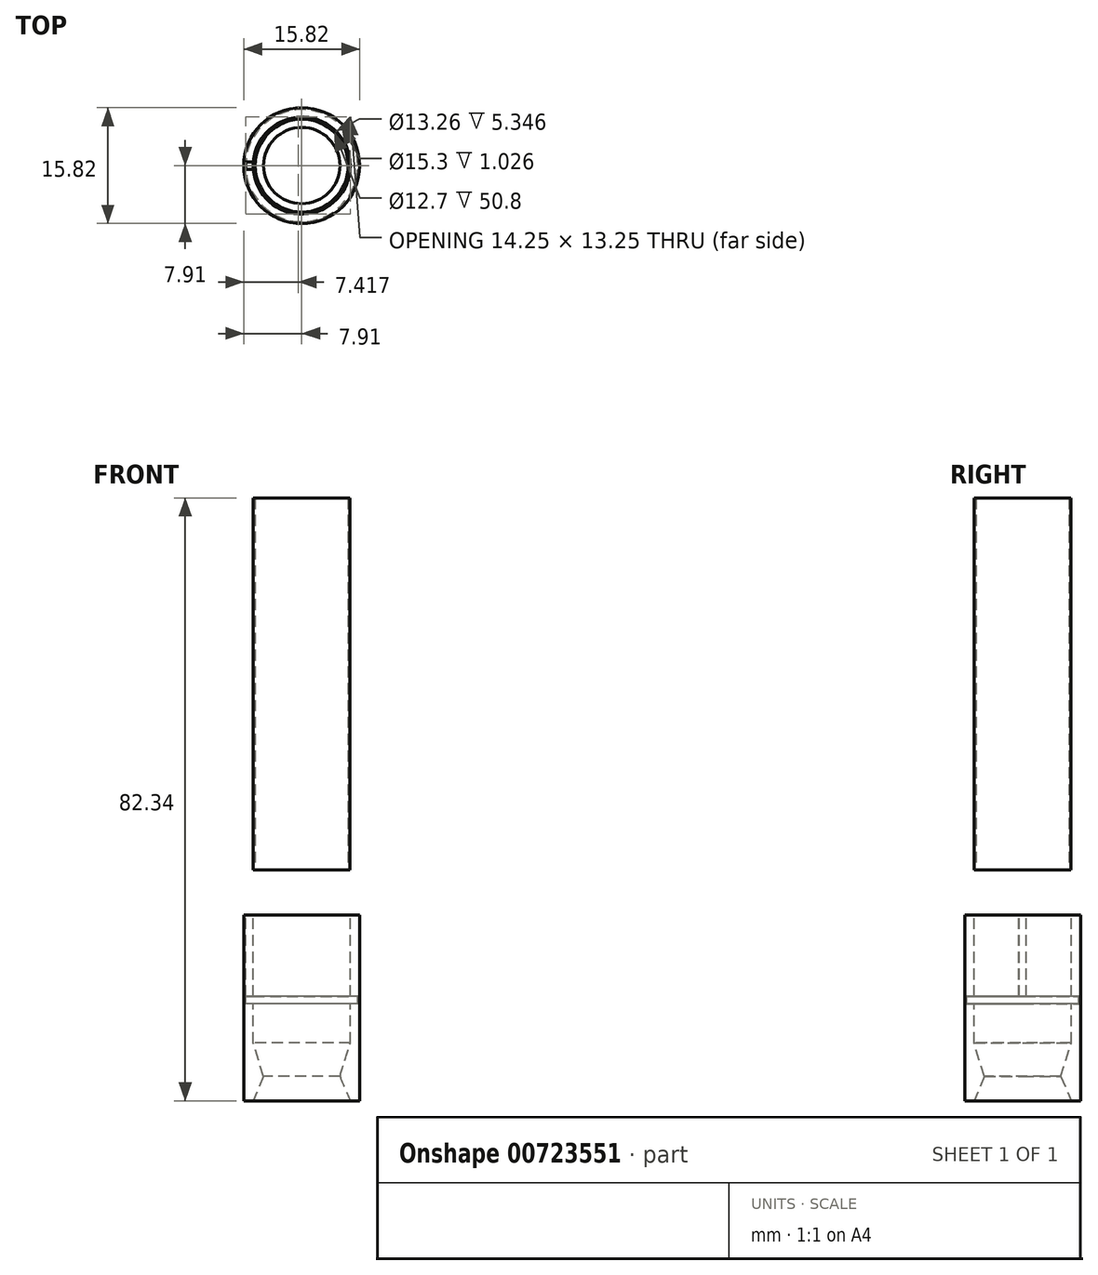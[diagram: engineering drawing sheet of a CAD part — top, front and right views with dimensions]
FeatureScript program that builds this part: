
annotation { "Feature Type Name" : "Feature", "Feature Type Description" : "" }
export const myFeature = defineFeature(function(context is Context, id is Id, definition is map)
    precondition{}
    {
        {
            var Q0;
            Q0=qCreatedBy(makeId("Top.planeOp"),FACE);
            var sketch = newSketch(context, id + "F0", { "sketchPlane" : qUnion([Q0])});
            skCircle(sketch, "E0", {"center": v(0, 0) * mm, "radius": 6.35 * mm});
            skSolve(sketch);
        }
        {
            var Q0;
            Q0=qCreatedBy(makeId("Front.planeOp"),FACE);
            var sketch = newSketch(context, id + "F1", { "sketchPlane" : qUnion([Q0])});
            skLineSegment(sketch, "E1", {"start": v(0, -60.7) * mm, "end": v(0, 70.56) * mm, "construction": true});
            skLineSegment(sketch, "E2", {"start": v(0, 70.56) * mm, "end": v(0, -60.7) * mm});
            skSolve(sketch);
        }
        {
            var Q0;
            Q0=makeQuery(id+"F0.imprint","IMPRINT",FACE,{"disambiguationData":[TD([[makeQuery(id+"F0.imprint","IMPRINT",EDGE,{"derivedFrom":sQuery(id+"F0.wireOp",EDGE,"E0")}),1.0]])]});
            var sketch = newSketch(context, id + "F2", { "sketchPlane" : qUnion([Q0])});
            skCircle(sketch, "E3.0", {"center": v(0, 0) * mm, "radius": 6.6 * mm});
            skSolve(sketch);
        }
        {
            var Q0;
            Q0=qCreatedBy(makeId("Front.planeOp"),FACE);
            var sketch = newSketch(context, id + "F3", { "sketchPlane" : qUnion([Q0])});
            skLineSegment(sketch, "E4", {"start": v(74.88, 0) * mm, "end": v(-75.82, 0) * mm, "construction": true});
            skSolve(sketch);
        }
        {
            var Q0;
            Q0=qCreatedBy(makeId("Front.planeOp"),FACE);
            var sketch = newSketch(context, id + "F4", { "sketchPlane" : qUnion([Q0])});
            skLineSegment(sketch, "E5", {"start": v(-6.63, -6.16) * mm, "end": v(-7.91, -6.16) * mm});
            skLineSegment(sketch, "E6", {"start": v(-7.91, -6.16) * mm, "end": v(-7.91, -31.54) * mm});
            skLineSegment(sketch, "E7", {"start": v(-7.91, -31.54) * mm, "end": v(-6.63, -31.54) * mm});
            skLineSegment(sketch, "E8", {"start": v(-6.63, -31.54) * mm, "end": v(-5.21, -28.22) * mm});
            skLineSegment(sketch, "E9", {"start": v(-5.21, -28.22) * mm, "end": v(-6.63, -23.65) * mm});
            skLineSegment(sketch, "E10", {"start": v(-6.63, -23.65) * mm, "end": v(-6.63, -18.3) * mm});
            skLineSegment(sketch, "E11", {"start": v(-6.63, -18.3) * mm, "end": v(-7.65, -18.3) * mm});
            skLineSegment(sketch, "E12", {"start": v(-7.65, -18.3) * mm, "end": v(-7.65, -17.28) * mm});
            skLineSegment(sketch, "E13", {"start": v(-7.65, -17.28) * mm, "end": v(-6.63, -17.28) * mm});
            skLineSegment(sketch, "E14", {"start": v(-6.63, -17.28) * mm, "end": v(-6.63, -6.16) * mm});
            skSolve(sketch);
        }
        {
            var Q0;
            Q0=makeQuery(id+"F4.imprint","IMPRINT",FACE,{"disambiguationData":[TD([[makeQuery(id+"F4.imprint","IMPRINT",EDGE,{"derivedFrom":sQuery(id+"F4.wireOp",EDGE,"E5")}),1.0]])]});
            var Q1;
            Q1=sQuery(id+"F1.wireOp",EDGE,"E2");
            revolve(context, id + "F5", {"surfaceOperationType" : NewSurfaceOperationType.NEW, "entities" : qUnion([Q0]), "axis" : qUnion([Q1]), "revolveType" : RevolveType.FULL});
        }
        {
            var Q0;
            Q0=makeQuery(id+"F2.imprint","IMPRINT",FACE,{"disambiguationData":[TD([[makeQuery(id+"F2.imprint","IMPRINT",EDGE,{"derivedFrom":sQuery(id+"F2.wireOp",EDGE,"E3.0")}),1.0]])]});
            extrude(context, id + "F6", {"entities" : qUnion([Q0]), "depth" : 50.8 * mm, "offsetDistance" : 25.4 * mm});
        }
        {
            var Q0;
            Q0=makeQuery(id+"F5.opRevolve","SWEPT_FACE",FACE,{"disambiguationData":[OSD([sQuery(id+"F4.wireOp",EDGE,"E5")])]});
            var sketch = newSketch(context, id + "F7", { "sketchPlane" : qUnion([Q0])});
            skLineSegment(sketch, "E15", {"start": v(0, 9.27) * mm, "end": v(0, -9.2) * mm, "construction": true});
            skSolve(sketch);
        }
        {
            var Q0;
            {var subQ0=sQuery(id+"F4.wireOp",EDGE,"E5");Q0=makeQuery(id+"F7.imprint","IMPRINT",FACE,{"disambiguationData":[TD([[makeQuery(id+"F7.imprint","IMPRINT",EDGE,{"derivedFrom":makeQuery(id+"F5.opRevolve","SWEPT_EDGE",EDGE,{"disambiguationData":[OSD([subQ0,sQuery(id+"F4.wireOp",EDGE,"E14")])]})}),-1.0]])]});}
            var sketch = newSketch(context, id + "F8", { "sketchPlane" : qUnion([Q0])});
            skLineSegment(sketch, "E16", {"start": v(-8.91, 0) * mm, "end": v(9.34, 0) * mm, "construction": true});
            skSolve(sketch);
        }
        {
            var Q0;
            {var subQ0=sQuery(id+"F4.wireOp",EDGE,"E5");Q0=makeQuery(id+"F8.imprint","IMPRINT",FACE,{"disambiguationData":[TD([[makeQuery(id+"F8.imprint","IMPRINT",EDGE,{"derivedFrom":makeQuery(id+"F7.imprint","IMPRINT",EDGE,{"derivedFrom":makeQuery(id+"F5.opRevolve","SWEPT_EDGE",EDGE,{"disambiguationData":[OSD([subQ0,sQuery(id+"F4.wireOp",EDGE,"E14")])]})})}),-1.0]])]});}
            var sketch = newSketch(context, id + "F9", { "sketchPlane" : qUnion([Q0])});
            skLineSegment(sketch, "E17", {"start": v(-6.6, 0.5) * mm, "end": v(-7.62, 0.5) * mm});
            skLineSegment(sketch, "E18", {"start": v(-7.62, 0.5) * mm, "end": v(-7.62, -0.5) * mm});
            skLineSegment(sketch, "E19", {"start": v(-7.62, -0.5) * mm, "end": v(-6.61, -0.5) * mm});
            skLineSegment(sketch, "E20", {"start": v(-6.61, -0.5) * mm, "end": v(-6.6, 0.5) * mm});
            skSolve(sketch);
        }
        {
            var Q0;
            {var subQ4=sQuery(id+"F9.wireOp",EDGE,"E18");Q0=makeQuery(id+"F9.imprint","IMPRINT",FACE,{"disambiguationData":[TD([[makeQuery(id+"F9.imprint","IMPRINT",EDGE,{"derivedFrom":subQ4}),1.0]])]});}
            extrude(context, id + "F10", {"entities" : qUnion([Q0]), "operationType" : NewBodyOperationType.REMOVE, "oppositeDirection" : true, "depth" : 12.12 * mm, "offsetDistance" : 25.4 * mm});
        }
    });
